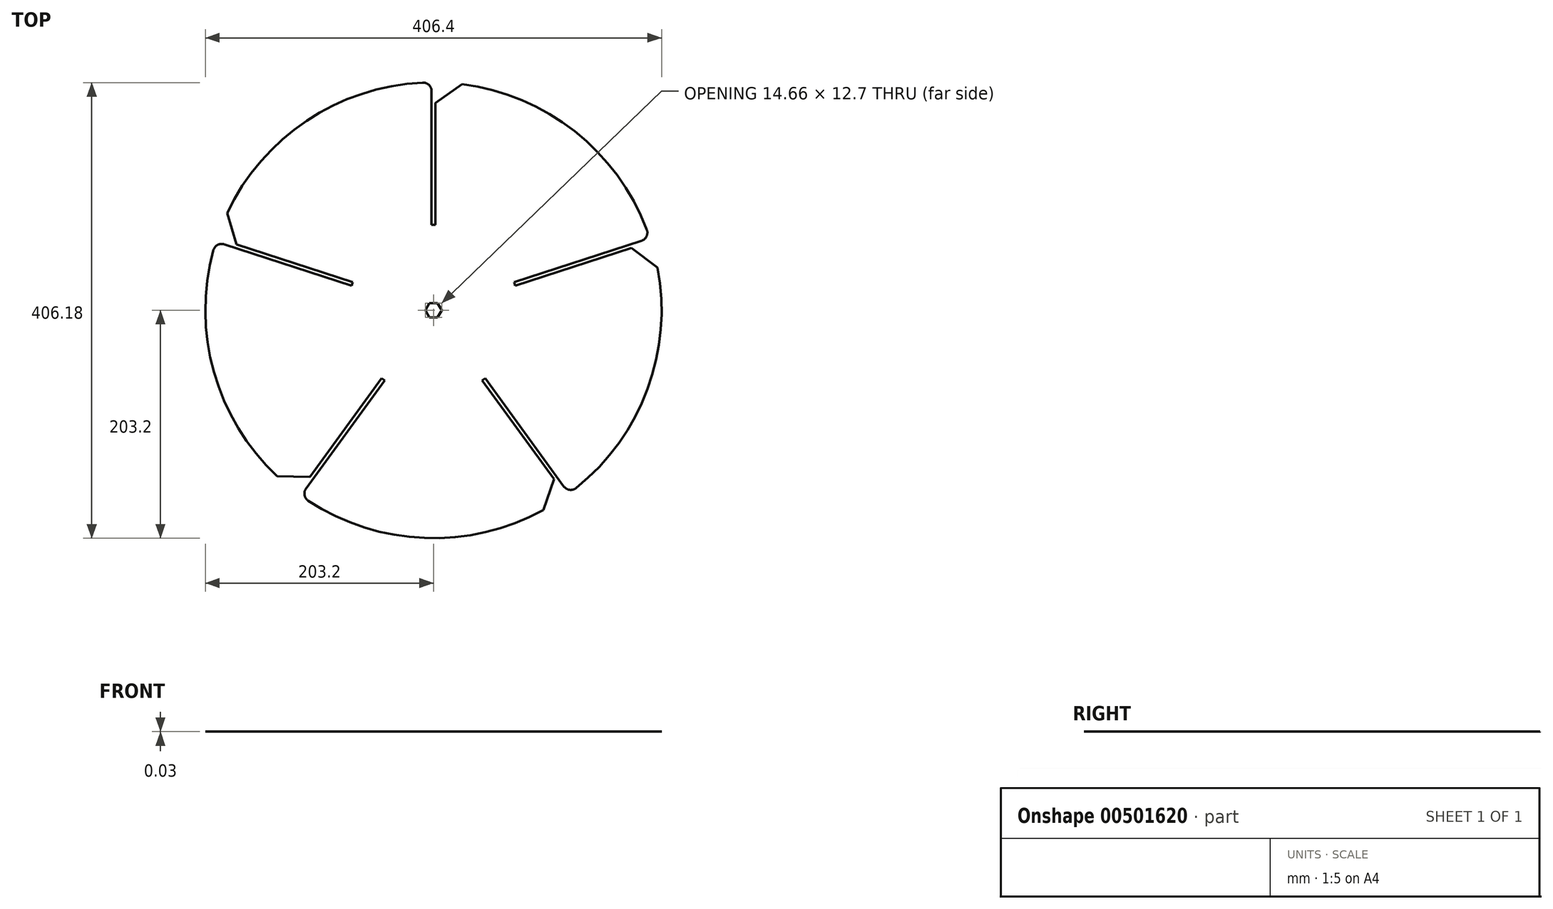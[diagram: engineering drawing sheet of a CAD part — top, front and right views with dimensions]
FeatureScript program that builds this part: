
annotation { "Feature Type Name" : "Feature", "Feature Type Description" : "" }
export const myFeature = defineFeature(function(context is Context, id is Id, definition is map)
    precondition{}
    {
        {
            var Q0;
            Q0=qCreatedBy(makeId("Top.planeOp"),FACE);
            var sketch = newSketch(context, id + "F0", { "sketchPlane" : qUnion([Q0])});
            skArc(sketch, "E0", {"start": v(-192.74, 64.36) * mm, "mid": v(188.61, -75.6) * mm, "end": v(-183.83, 86.58) * mm});
            skArc(sketch, "E1.cCircle", {"start": v(-192.74, 64.36) * mm, "mid": v(-197.03, -49.7) * mm, "end": v(-139.15, -148.08) * mm, "construction": true});
            skLineSegment(sketch, "E1.0", {"start": v(147.63, -203.2) * mm, "end": v(-147.63, -203.2) * mm, "construction": true});
            skLineSegment(sketch, "E1.1", {"start": v(-147.63, -203.2) * mm, "end": v(-238.88, 77.62) * mm, "construction": true});
            skLineSegment(sketch, "E1.2", {"start": v(-238.88, 77.62) * mm, "end": v(0, 251.17) * mm, "construction": true});
            skLineSegment(sketch, "E1.3", {"start": v(0, 251.17) * mm, "end": v(238.88, 77.62) * mm, "construction": true});
            skLineSegment(sketch, "E1.4", {"start": v(238.88, 77.62) * mm, "end": v(147.63, -203.2) * mm, "construction": true});
            skPoint(sketch, "E1.0.midPoint", {"position": v(0, -203.2) * mm});
            skLineSegment(sketch, "E2", {"start": v(0, 251.17) * mm, "end": v(0, 0) * mm, "construction": true});
            skLineSegment(sketch, "E3", {"start": v(-238.88, 77.62) * mm, "end": v(0, 0) * mm, "construction": true});
            skLineSegment(sketch, "E4", {"start": v(-147.63, -203.2) * mm, "end": v(0, 0) * mm, "construction": true});
            skLineSegment(sketch, "E5", {"start": v(147.63, -203.2) * mm, "end": v(0, 0) * mm, "construction": true});
            skLineSegment(sketch, "E6", {"start": v(238.88, 77.62) * mm, "end": v(0, 0) * mm, "construction": true});
            skLineSegment(sketch, "E7.bottom", {"start": v(1.65, 76.2) * mm, "end": v(-1.65, 76.2) * mm});
            skLineSegment(sketch, "E7.top", {"start": v(1.65, 228.6) * mm, "end": v(-1.65, 228.6) * mm});
            skLineSegment(sketch, "E7.left", {"start": v(1.65, 76.2) * mm, "end": v(1.65, 228.6) * mm});
            skLineSegment(sketch, "E7.right", {"start": v(-1.65, 76.2) * mm, "end": v(-1.65, 228.6) * mm});
            skPoint(sketch, "E7.middle", {"position": v(0, 152.4) * mm});
            skLineSegment(sketch, "E8", {"start": v(0, 0) * mm, "end": v(119.44, 164.4) * mm, "construction": true});
            skLineSegment(sketch, "E9.MirrorCS", {"start": v(216.9, 72.21) * mm, "end": v(217.92, 69.07) * mm});
            skLineSegment(sketch, "E10.MirrorCS", {"start": v(71.96, 25.12) * mm, "end": v(216.9, 72.21) * mm});
            skLineSegment(sketch, "E11.MirrorCS", {"start": v(72.98, 21.98) * mm, "end": v(217.92, 69.07) * mm});
            skLineSegment(sketch, "E12.MirrorCS", {"start": v(71.96, 25.12) * mm, "end": v(72.98, 21.98) * mm});
            skLineSegment(sketch, "E13.MirrorCS", {"start": v(0, 0) * mm, "end": v(193.25, -62.8) * mm, "construction": true});
            skLineSegment(sketch, "E14.MirrorCS", {"start": v(0, 0) * mm, "end": v(0, -203.2) * mm, "construction": true});
            skLineSegment(sketch, "E15.MirrorCS", {"start": v(0, 0) * mm, "end": v(-193.25, -62.8) * mm, "construction": true});
            skLineSegment(sketch, "E16.MirrorCS", {"start": v(0, 0) * mm, "end": v(-119.44, 164.4) * mm, "construction": true});
            skLineSegment(sketch, "E17.MirrorCS", {"start": v(43.45, -62.62) * mm, "end": v(133.03, -185.91) * mm});
            skLineSegment(sketch, "E18.MirrorCS", {"start": v(46.12, -60.68) * mm, "end": v(135.7, -183.97) * mm});
            skLineSegment(sketch, "E19.MirrorCS", {"start": v(43.45, -62.62) * mm, "end": v(46.12, -60.68) * mm});
            skLineSegment(sketch, "E20.MirrorCS", {"start": v(133.03, -185.91) * mm, "end": v(135.7, -183.97) * mm});
            skLineSegment(sketch, "E21.MirrorCS", {"start": v(-43.45, -62.62) * mm, "end": v(-46.12, -60.68) * mm});
            skLineSegment(sketch, "E22.MirrorCS", {"start": v(-46.12, -60.68) * mm, "end": v(-135.7, -183.97) * mm});
            skLineSegment(sketch, "E23.MirrorCS", {"start": v(-43.45, -62.62) * mm, "end": v(-133.03, -185.91) * mm});
            skLineSegment(sketch, "E24.MirrorCS", {"start": v(-133.03, -185.91) * mm, "end": v(-135.7, -183.97) * mm});
            skLineSegment(sketch, "E25.MirrorCS", {"start": v(-71.96, 25.12) * mm, "end": v(-72.98, 21.98) * mm});
            skLineSegment(sketch, "E26.MirrorCS", {"start": v(-71.96, 25.12) * mm, "end": v(-216.9, 72.21) * mm});
            skLineSegment(sketch, "E27.MirrorCS", {"start": v(-72.98, 21.98) * mm, "end": v(-217.92, 69.07) * mm});
            skLineSegment(sketch, "E28.MirrorCS", {"start": v(-216.9, 72.21) * mm, "end": v(-217.92, 69.07) * mm});
            skLineSegment(sketch, "E29", {"start": v(-183.83, 86.58) * mm, "end": v(-175.31, 58.7) * mm});
            skLineSegment(sketch, "E30.1.0", {"start": v(25.53, 201.59) * mm, "end": v(1.65, 184.87) * mm});
            skLineSegment(sketch, "E30.2.0", {"start": v(199.61, 38.01) * mm, "end": v(176.33, 55.56) * mm});
            skLineSegment(sketch, "E30.3.0", {"start": v(97.84, -178.1) * mm, "end": v(107.33, -150.53) * mm});
            skLineSegment(sketch, "E30.4.0", {"start": v(-139.15, -148.08) * mm, "end": v(-110, -148.6) * mm});
            skLineSegment(sketch, "E30.anchor1", {"start": v(0, 0) * mm, "end": v(-175.31, 58.7) * mm, "construction": true});
            skLineSegment(sketch, "E30.anchor2", {"start": v(0, 0) * mm, "end": v(-110, -148.6) * mm, "construction": true});
            skArc(sketch, "E31.trimOffspring", {"start": v(-120.77, -163.42) * mm, "mid": v(197.03, 49.7) * mm, "end": v(-183.83, 86.58) * mm, "construction": true});
            skSolve(sketch);
        }
        {
            var Q0;
            {var subQ24=sQuery(id+"F0.wireOp",EDGE,"E7.bottom");Q0=makeQuery(id+"F0.imprint","IMPRINT",FACE,{"disambiguationData":[TD([[makeQuery(id+"F0.imprint","IMPRINT",EDGE,{"derivedFrom":subQ24}),1.0]])]});}
            extrude(context, id + "F1", {"entities" : qUnion([Q0]), "depth" : 3 / 101.6 * mm});
        }
        {
            var Q0;
            Q0=makeQuery(id+"F1.opExtrude","CAP_FACE",FACE,{"disambiguationData":[OSD([sQuery(id+"F0.wireOp",EDGE,"E0"),sQuery(id+"F0.wireOp",EDGE,"E7.bottom"),sQuery(id+"F0.wireOp",EDGE,"E7.left"),sQuery(id+"F0.wireOp",EDGE,"E7.right"),sQuery(id+"F0.wireOp",EDGE,"E10.MirrorCS"),sQuery(id+"F0.wireOp",EDGE,"E11.MirrorCS"),sQuery(id+"F0.wireOp",EDGE,"E12.MirrorCS"),sQuery(id+"F0.wireOp",EDGE,"E17.MirrorCS"),sQuery(id+"F0.wireOp",EDGE,"E18.MirrorCS"),sQuery(id+"F0.wireOp",EDGE,"E19.MirrorCS"),sQuery(id+"F0.wireOp",EDGE,"E21.MirrorCS"),sQuery(id+"F0.wireOp",EDGE,"E22.MirrorCS"),sQuery(id+"F0.wireOp",EDGE,"E23.MirrorCS"),sQuery(id+"F0.wireOp",EDGE,"E25.MirrorCS"),sQuery(id+"F0.wireOp",EDGE,"E26.MirrorCS"),sQuery(id+"F0.wireOp",EDGE,"E27.MirrorCS"),sQuery(id+"F0.wireOp",EDGE,"E29"),sQuery(id+"F0.wireOp",EDGE,"E30.1.0"),sQuery(id+"F0.wireOp",EDGE,"E30.2.0"),sQuery(id+"F0.wireOp",EDGE,"E30.3.0"),sQuery(id+"F0.wireOp",EDGE,"E30.4.0")])],"isStart":false});
            var sketch = newSketch(context, id + "F2", { "sketchPlane" : qUnion([Q0])});
            skCircle(sketch, "E32.cCircle", {"center": v(0, 0) * mm, "radius": 6.35 * mm, "construction": true});
            skLineSegment(sketch, "E32.0", {"start": v(-3.67, 6.35) * mm, "end": v(3.67, 6.35) * mm});
            skLineSegment(sketch, "E32.1", {"start": v(3.67, 6.35) * mm, "end": v(7.33, 0) * mm});
            skLineSegment(sketch, "E32.2", {"start": v(7.33, 0) * mm, "end": v(3.67, -6.35) * mm});
            skLineSegment(sketch, "E32.3", {"start": v(3.67, -6.35) * mm, "end": v(-3.67, -6.35) * mm});
            skLineSegment(sketch, "E32.4", {"start": v(-3.67, -6.35) * mm, "end": v(-7.33, 0) * mm});
            skLineSegment(sketch, "E32.5", {"start": v(-7.33, 0) * mm, "end": v(-3.67, 6.35) * mm});
            skPoint(sketch, "E32.0.midPoint", {"position": v(0, 6.35) * mm});
            skSolve(sketch);
        }
        {
            var Q0;
            Q0=qSketchRegion(id+"F2",true);
            var Q1;
            Q1=makeQuery(id+"F1.opExtrude","CAP_FACE",FACE,{"disambiguationData":[OSD([sQuery(id+"F0.wireOp",EDGE,"E0"),sQuery(id+"F0.wireOp",EDGE,"E7.bottom"),sQuery(id+"F0.wireOp",EDGE,"E7.left"),sQuery(id+"F0.wireOp",EDGE,"E7.right"),sQuery(id+"F0.wireOp",EDGE,"E10.MirrorCS"),sQuery(id+"F0.wireOp",EDGE,"E11.MirrorCS"),sQuery(id+"F0.wireOp",EDGE,"E12.MirrorCS"),sQuery(id+"F0.wireOp",EDGE,"E17.MirrorCS"),sQuery(id+"F0.wireOp",EDGE,"E18.MirrorCS"),sQuery(id+"F0.wireOp",EDGE,"E19.MirrorCS"),sQuery(id+"F0.wireOp",EDGE,"E21.MirrorCS"),sQuery(id+"F0.wireOp",EDGE,"E22.MirrorCS"),sQuery(id+"F0.wireOp",EDGE,"E23.MirrorCS"),sQuery(id+"F0.wireOp",EDGE,"E25.MirrorCS"),sQuery(id+"F0.wireOp",EDGE,"E26.MirrorCS"),sQuery(id+"F0.wireOp",EDGE,"E27.MirrorCS"),sQuery(id+"F0.wireOp",EDGE,"E29"),sQuery(id+"F0.wireOp",EDGE,"E30.1.0"),sQuery(id+"F0.wireOp",EDGE,"E30.2.0"),sQuery(id+"F0.wireOp",EDGE,"E30.3.0"),sQuery(id+"F0.wireOp",EDGE,"E30.4.0")])],"isStart":true});
            extrude(context, id + "F3", {"entities" : qUnion([Q0]), "operationType" : NewBodyOperationType.REMOVE, "endBound" : BoundingType.UP_TO_SURFACE, "oppositeDirection" : true, "endBoundEntityFace" : qUnion([Q1]), "depth" : 25.4 * mm});
        }
        {
            var Q0;
            Q0=makeQuery(id+"F1.opExtrude","SWEPT_EDGE",EDGE,{"disambiguationData":[OSD([sQuery(id+"F0.wireOp",EDGE,"E0"),sQuery(id+"F0.wireOp",EDGE,"E27.MirrorCS")])]});
            var Q1;
            Q1=makeQuery(id+"F1.opExtrude","SWEPT_EDGE",EDGE,{"disambiguationData":[OSD([sQuery(id+"F0.wireOp",EDGE,"E0"),sQuery(id+"F0.wireOp",EDGE,"E7.right")])]});
            var Q2;
            Q2=makeQuery(id+"F1.opExtrude","SWEPT_EDGE",EDGE,{"disambiguationData":[OSD([sQuery(id+"F0.wireOp",EDGE,"E0"),sQuery(id+"F0.wireOp",EDGE,"E10.MirrorCS")])]});
            var Q3;
            Q3=makeQuery(id+"F1.opExtrude","SWEPT_EDGE",EDGE,{"disambiguationData":[OSD([sQuery(id+"F0.wireOp",EDGE,"E0"),sQuery(id+"F0.wireOp",EDGE,"E18.MirrorCS")])]});
            var Q4;
            Q4=makeQuery(id+"F1.opExtrude","SWEPT_EDGE",EDGE,{"disambiguationData":[OSD([sQuery(id+"F0.wireOp",EDGE,"E0"),sQuery(id+"F0.wireOp",EDGE,"E23.MirrorCS")])]});
            fillet(context, id + "F4", {"entities" : qUnion([Q0, Q1, Q2, Q3, Q4]), "radius" : 7.62 * mm, "tangentPropagation" : true, "allowEdgeOverflow" : false});
        }
    });
